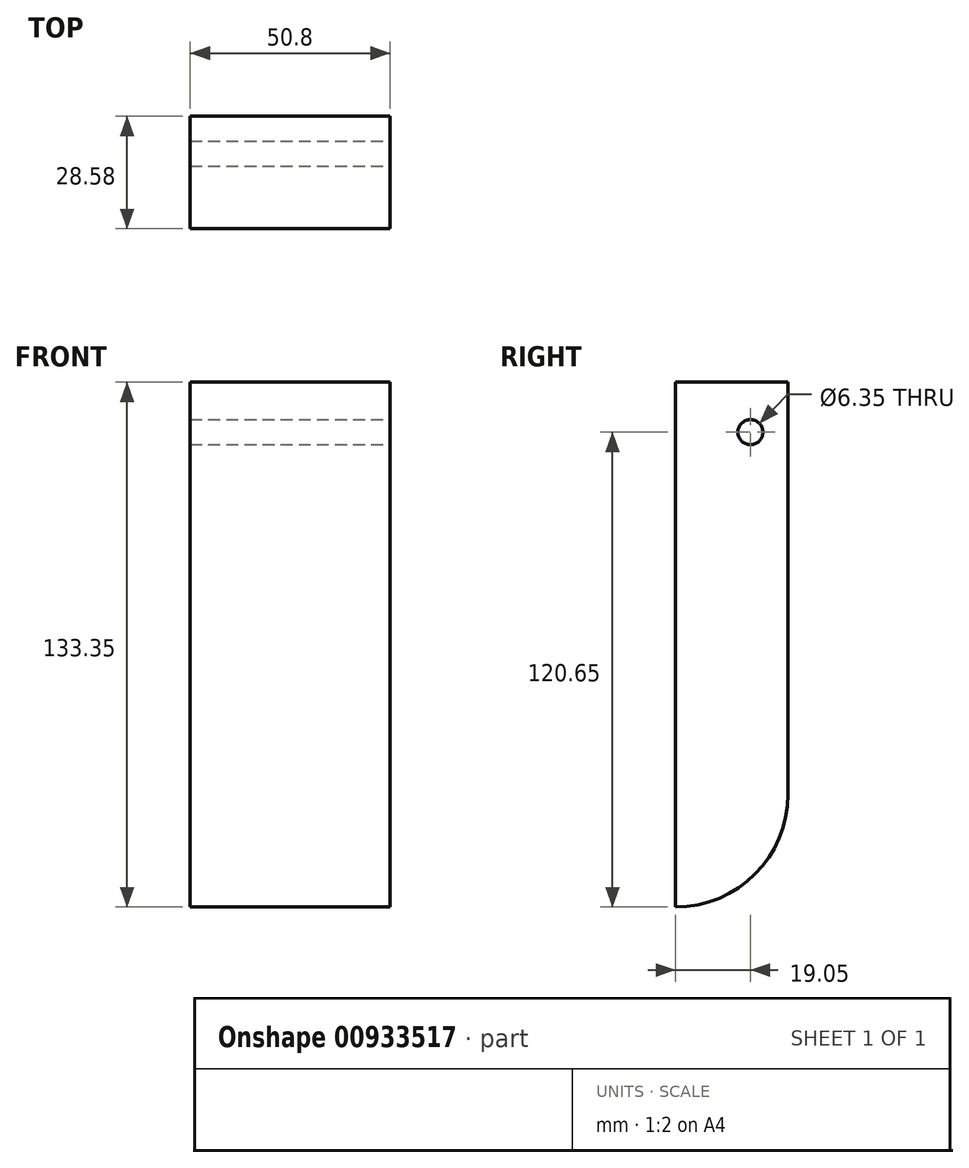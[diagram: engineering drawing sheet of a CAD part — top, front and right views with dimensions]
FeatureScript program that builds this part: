
annotation { "Feature Type Name" : "Feature", "Feature Type Description" : "" }
export const myFeature = defineFeature(function(context is Context, id is Id, definition is map)
    precondition{}
    {
        {
            var Q0;
            Q0=qCreatedBy(makeId("Right.planeOp"),FACE);
            var sketch = newSketch(context, id + "F0", { "sketchPlane" : qUnion([Q0])});
            skLineSegment(sketch, "E0", {"start": v(0, 0) * mm, "end": v(0, 133.35) * mm});
            skLineSegment(sketch, "E1", {"start": v(0, 133.35) * mm, "end": v(28.57, 133.35) * mm});
            skLineSegment(sketch, "E2", {"start": v(28.57, 133.35) * mm, "end": v(28.58, 28.58) * mm});
            skArc(sketch, "E3", {"start": v(28.58, 28.58) * mm, "mid": v(20.2, 8.37) * mm, "end": v(0, 0) * mm});
            skSolve(sketch);
        }
        {
            var Q0;
            Q0 = qSketchRegion(id + "F0", true);
            extrude(context, id + "F1", {"entities" : qUnion([Q0]), "depth" : 50.8 * mm, "offsetDistance" : 25.4 * mm});
        }
        {
            var Q0;
            Q0=makeQuery(id+"F1.opExtrude","CAP_FACE",FACE,{"disambiguationData":[OSD([sQuery(id+"F0.wireOp",EDGE,"E0"),sQuery(id+"F0.wireOp",EDGE,"E1"),sQuery(id+"F0.wireOp",EDGE,"E2"),sQuery(id+"F0.wireOp",EDGE,"E3")])],"isStart":false});
            var sketch = newSketch(context, id + "F2", { "sketchPlane" : qUnion([Q0])});
            skPoint(sketch, "E4", {"position": v(19.05, 120.65) * mm});
            skSolve(sketch);
        }
        {
            var Q0;
            Q0=sQuery(id+"F2.wireOp",VERTEX,"E4");
            var Q1;
            Q1=makeQuery(id+"F1.opExtrude","SWEPT_BODY",BODY,{"disambiguationData":[OSD([sQuery(id+"F0.wireOp",EDGE,"E0"),sQuery(id+"F0.wireOp",EDGE,"E1"),sQuery(id+"F0.wireOp",EDGE,"E2"),sQuery(id+"F0.wireOp",EDGE,"E3")])]});
            hole(context, id + "F3", {"style" : HoleStyle.SIMPLE, "endStyle" : HoleEndStyle.THROUGH, "holeDiameter" : 6.35 * mm, "majorDiameter" : 6.35 * mm, "isTappedThrough" : true, "tappedDepth" : 12.7 * mm, "tapClearance" : 3, "locations" : qUnion([Q0]), "scope" : qUnion([Q1])});
        }
    });
